# Revit family: 2059410 Sylvania Lighting Fixture ASCENT 150 II SQ 3500 4K STD EM
name_source: partatom
category: Lighting Fixtures
revit_build: Autodesk Revit 2016 (Build: 20150220_1215(x64)
units: mm (PartAtom-declared; Revit-internal decimal feet)

## family parameters
Cut with Voids When Loaded = No
Host = Face
Light Source = Yes
OmniClass Number = 23.80.70.11.17
OmniClass Title = Specialized Lighting by Location or Use
Part Type = Normal
Room Calculation Point = No
Round Connector Dimension = Use Diameter
Shared = No

## types (2) — shared parameters
Assembly Code = D5020200
AssetType = Fixed
Color Filter = 16777215
Description = The ASCENT 150 II SQ 3500 4K STD EM  is a high efficient downlight luminaire with luminous flux: 3512lm, luminaire efficacy: 125lm/W, Colour rendering index Ra >80, Colour temperature: 4000K Warm white, Average life rated at 50,000Hrs, Class II, Protection rating IP44/IK02, Cut out dimensions: 175mm, Weight: 2.45kg
Dimming Lamp Color Temperature Shift = <None>
DocumentationLiterature = http://www.sylvania-lighting.com
DurationUnit = hours
ElectricShockClassification = Class II
Emit Shape Visible in Rendering = No
Emit from Rectangle Length = 154 mm
Emit from Rectangle Width = 154 mm
ExpectedLife = 50000
Height_SYL = 158 mm
IfcExportAs = IfcLightFixtureType
IfcExportType = IfcLightFixtureType
ImpactProtectionIndex = IK02
IngressProtection = IP44
Keynote = 16500
Lamp = LED
LampColourRenderingIndex = 80
LampColourTemperature = 4000 K
LampsType = LED
Length_SYL = 188 mm  [stored 0.616798 ft]
LightOutputRatio = 100
LuminousEfficacy = 125 lm/W
Manufacturer = Feilo Sylvania
ManufacturerName = Feilo Sylvania
Material = aluminium housing
Material_1_SYL = Stainless Steel_Acc_Sylvania_White
Material_2_SYL = Aluminium_Reflector_Sylvania
Material_3_SYL = Stainless Steel_Body_Sylvania_Black
Material_4_SYL = LED_Sylvania
Model = ASCENT 150 II SQ 3500 4K STD EM
ModelNumber = 2059410
ModelReference = ASCENT 150 II SQ 3500 4K STD EM
Name = ASCENT 150 II SQ 3500 4K STD EM
NominalHeight = 158 mm
PowerConsumption = 28 W
Tilt Angle = -90.00°
TypeName = ASCENT 150 II SQ 3500 4K STD EM
URL = http://www.sylvania-lighting.com
Voltage = 0 V
Weight = 2.45 kg
Width_SYL = 188 mm  [stored 0.616798 ft]
zero-valued in all types: Default Elevation, NominalLength, NominalWidth, PowerFactor

## per-type parameters (varying)
| type | Apparent Load | LampNominalLuminous | Photometric Web File |
| 2059410 ASCENT 150 II SQ 3500 4K STD EM | 28 VA | 3512 lm | 2059410.ies |
| 2059410 ASCENT 150 II SQ 3500 4K STD EM Emergency mode | 3 VA | 430 lm | 2059410EM.ies |

note: [stored X ft] marks values corroborated as IEEE doubles in the binary element streams (Revit-internal decimal feet)

## geometry (parser evidence)
native form markers: Sweep x3
no freeform markers — native parametric forms only
